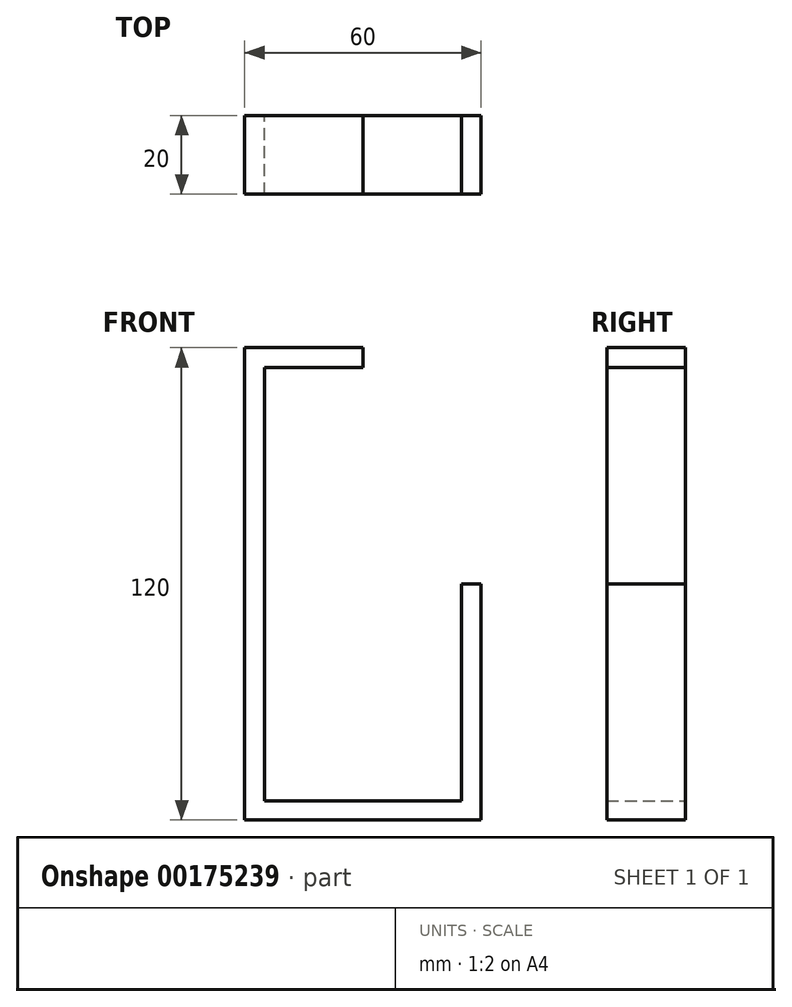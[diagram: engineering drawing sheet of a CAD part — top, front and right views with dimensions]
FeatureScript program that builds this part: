
annotation { "Feature Type Name" : "Feature", "Feature Type Description" : "" }
export const myFeature = defineFeature(function(context is Context, id is Id, definition is map)
    precondition{}
    {
        {
            var Q0;
            Q0=qCreatedBy(makeId("Front.planeOp"),FACE);
            var sketch = newSketch(context, id + "F0", { "sketchPlane" : qUnion([Q0])});
            skPoint(sketch, "E0.start.orphan", {"position": v(0, 73.6) * mm});
            skLineSegment(sketch, "E1", {"start": v(0, 73.6) * mm, "end": v(0, -74.33) * mm});
            skLineSegment(sketch, "E2", {"start": v(0, 0) * mm, "end": v(-30, 0) * mm});
            skLineSegment(sketch, "E3", {"start": v(-30, 0) * mm, "end": v(-30, -60) * mm});
            skLineSegment(sketch, "E4", {"start": v(-30, -60) * mm, "end": v(0, -60) * mm});
            skLineSegment(sketch, "E5", {"start": v(-30, 0) * mm, "end": v(-30, 60) * mm});
            skLineSegment(sketch, "E6", {"start": v(-30, 60) * mm, "end": v(0, 60) * mm});
            skLineSegment(sketch, "E7", {"start": v(0, 60) * mm, "end": v(0, 55) * mm});
            skLineSegment(sketch, "E8", {"start": v(0, 55) * mm, "end": v(-25, 55) * mm});
            skLineSegment(sketch, "E9", {"start": v(-25, 59.8) * mm, "end": v(-25, -55.2) * mm});
            skLineSegment(sketch, "E10", {"start": v(-25, -55.2) * mm, "end": v(0, -55.2) * mm});
            skLineSegment(sketch, "E11.MirrorCS", {"start": v(30, 60) * mm, "end": v(0, 60) * mm});
            skLineSegment(sketch, "E12.MirrorCS", {"start": v(25, -55.2) * mm, "end": v(0, -55.2) * mm});
            skLineSegment(sketch, "E13.MirrorCS", {"start": v(0, 0) * mm, "end": v(30, 0) * mm});
            skLineSegment(sketch, "E14.MirrorCS", {"start": v(0, 55) * mm, "end": v(25, 55) * mm});
            skLineSegment(sketch, "E15.MirrorCS", {"start": v(30, 0) * mm, "end": v(30, -60) * mm});
            skLineSegment(sketch, "E16.MirrorCS", {"start": v(30, 0) * mm, "end": v(30, 60) * mm});
            skLineSegment(sketch, "E17.MirrorCS", {"start": v(30, -60) * mm, "end": v(0, -60) * mm});
            skLineSegment(sketch, "E18.MirrorCS", {"start": v(25, 59.8) * mm, "end": v(25, -55.2) * mm});
            skSolve(sketch);
        }
        {
            var Q0;
            Q0=qCreatedBy(makeId("Front.planeOp"),FACE);
            var sketch = newSketch(context, id + "F1", { "sketchPlane" : qUnion([Q0])});
            skSolve(sketch);
        }
        {
            var Q0;
            Q0 = qSketchRegion(id + "F1", true);
            var Q1;
            {var subQ2=sQuery(id+"F0.wireOp",EDGE,"E3");Q1=makeQuery(id+"F0.imprint","IMPRINT",FACE,{"disambiguationData":[TD([[makeQuery(id+"F0.imprint","IMPRINT",EDGE,{"derivedFrom":subQ2}),1.0]])]});}
            var Q2;
            {var subQ0=sQuery(id+"F0.wireOp",EDGE,"E5");Q2=makeQuery(id+"F0.imprint","IMPRINT",FACE,{"disambiguationData":[TD([[makeQuery(id+"F0.imprint","IMPRINT",EDGE,{"derivedFrom":subQ0}),-1.0]])]});}
            var Q3;
            Q3=makeQuery(id+"F0.imprint","IMPRINT",FACE,{"disambiguationData":[TD([[makeQuery(id+"F0.imprint","IMPRINT",EDGE,{"derivedFrom":sQuery(id+"F0.wireOp",EDGE,"E7")}),1.0]])]});
            var Q4;
            {var subQ1=sQuery(id+"F0.wireOp",EDGE,"E15.MirrorCS");Q4=makeQuery(id+"F0.imprint","IMPRINT",FACE,{"disambiguationData":[TD([[makeQuery(id+"F0.imprint","IMPRINT",EDGE,{"derivedFrom":subQ1}),-1.0]])]});}
            extrude(context, id + "F2", {"entities" : qUnion([Q0, Q1, Q2, Q3, Q4]), "depth" : 20 * mm});
        }
    });
